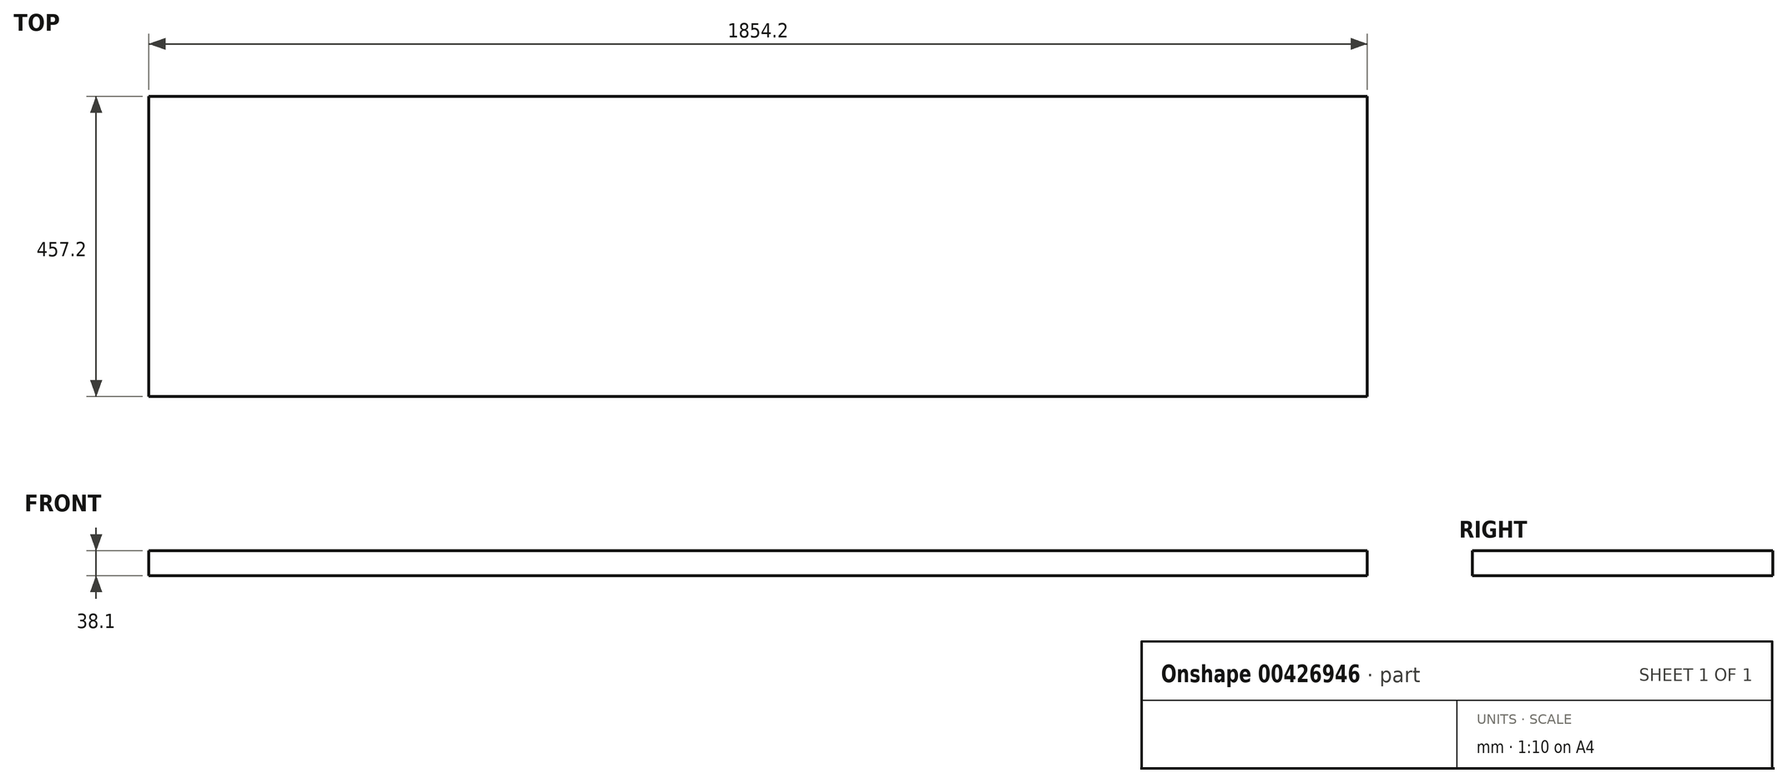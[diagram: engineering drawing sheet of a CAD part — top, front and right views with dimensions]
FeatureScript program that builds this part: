
annotation { "Feature Type Name" : "Feature", "Feature Type Description" : "" }
export const myFeature = defineFeature(function(context is Context, id is Id, definition is map)
    precondition{}
    {
        {
            var Q0;
            Q0=qCreatedBy(makeId("Top.planeOp"),FACE);
            var sketch = newSketch(context, id + "F0", { "sketchPlane" : qUnion([Q0])});
            skLineSegment(sketch, "E0.bottom", {"start": v(0, 0) * mm, "end": v(-1854.2, 0) * mm});
            skLineSegment(sketch, "E0.top", {"start": v(0, -457.2) * mm, "end": v(-1854.2, -457.2) * mm});
            skLineSegment(sketch, "E0.left", {"start": v(0, 0) * mm, "end": v(0, -457.2) * mm});
            skLineSegment(sketch, "E0.right", {"start": v(-1854.2, 0) * mm, "end": v(-1854.2, -457.2) * mm});
            skSolve(sketch);
        }
        {
            var Q0;
            Q0=makeQuery(id+"F0.imprint","IMPRINT",FACE,{"disambiguationData":[TD([[makeQuery(id+"F0.imprint","IMPRINT",EDGE,{"derivedFrom":sQuery(id+"F0.wireOp",EDGE,"E0.bottom")}),1.0]])]});
            extrude(context, id + "F1", {"entities" : qUnion([Q0]), "depth" : 38.1 * mm});
        }
    });
